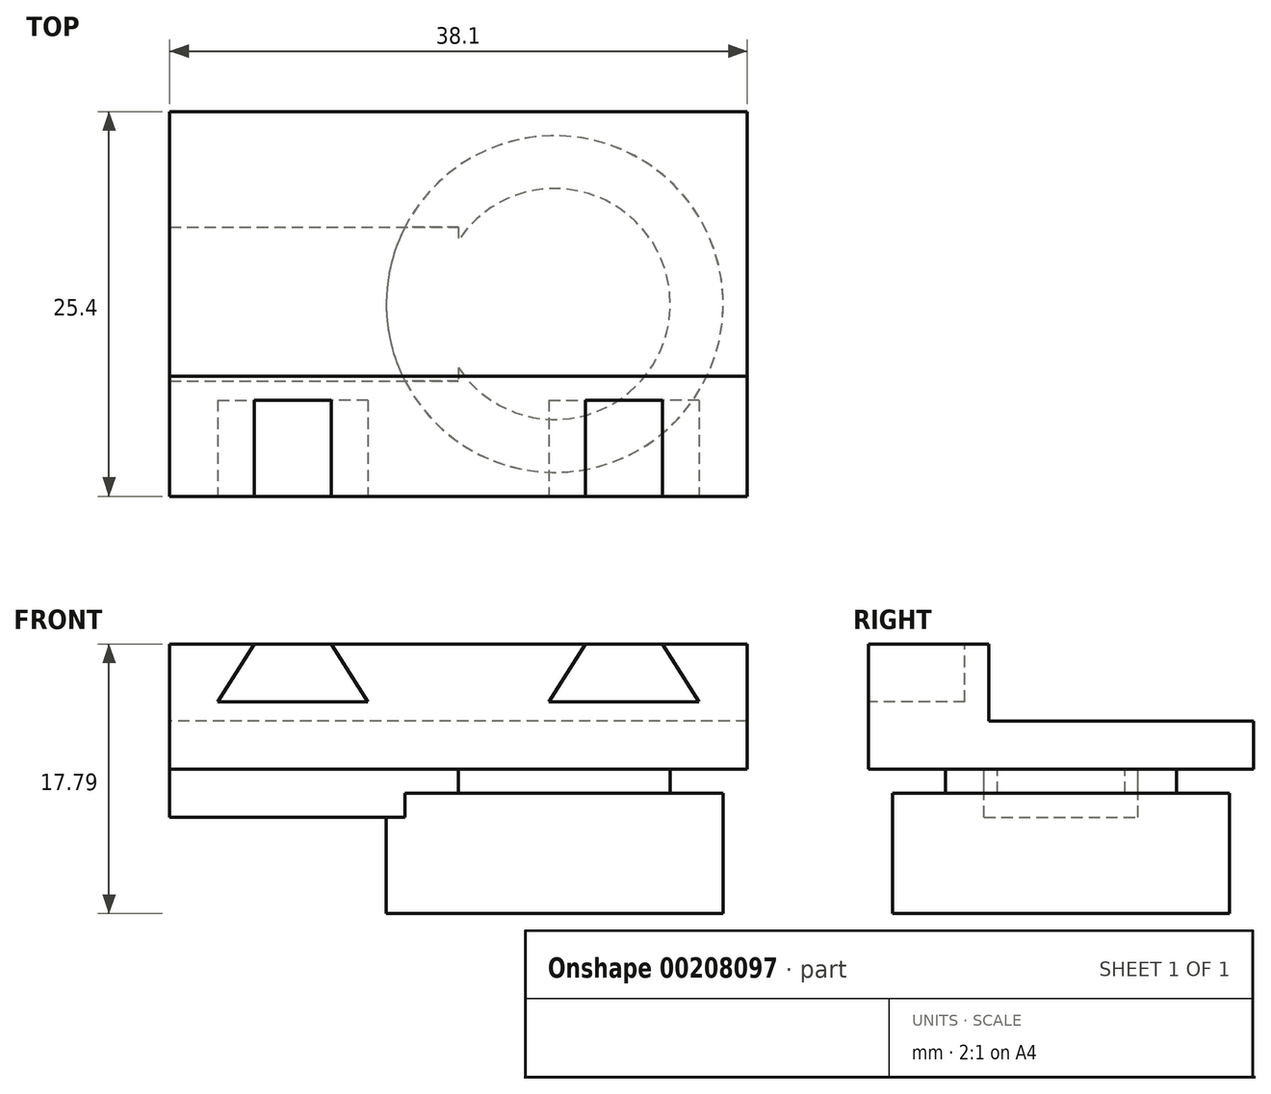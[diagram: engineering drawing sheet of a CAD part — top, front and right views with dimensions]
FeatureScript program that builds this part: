
annotation { "Feature Type Name" : "Feature", "Feature Type Description" : "" }
export const myFeature = defineFeature(function(context is Context, id is Id, definition is map)
    precondition{}
    {
        {
            var Q0;
            Q0=qCreatedBy(makeId("Top.planeOp"),FACE);
            var sketch = newSketch(context, id + "F0", { "sketchPlane" : qUnion([Q0])});
            skLineSegment(sketch, "E0.bottom", {"start": v(0, 0) * mm, "end": v(-38.1, 0) * mm});
            skLineSegment(sketch, "E0.top", {"start": v(0, 25.4) * mm, "end": v(-38.1, 25.4) * mm});
            skLineSegment(sketch, "E0.left", {"start": v(0, 0) * mm, "end": v(0, 25.4) * mm});
            skLineSegment(sketch, "E0.right", {"start": v(-38.1, 0) * mm, "end": v(-38.1, 25.4) * mm});
            skSolve(sketch);
        }
        {
            var Q0;
            Q0=makeQuery(id+"F0.imprint","IMPRINT",FACE,{"disambiguationData":[TD([[makeQuery(id+"F0.imprint","IMPRINT",EDGE,{"derivedFrom":sQuery(id+"F0.wireOp",EDGE,"E0.bottom")}),-1.0]])]});
            extrude(context, id + "F1", {"entities" : qUnion([Q0]), "depth" : 3.17 * mm});
        }
        {
            var Q0;
            Q0=makeQuery(id+"F1.opExtrude","SWEPT_FACE",FACE,{"disambiguationData":[OSD([sQuery(id+"F0.wireOp",EDGE,"E0.bottom")])]});
            var sketch = newSketch(context, id + "F2", { "sketchPlane" : qUnion([Q0])});
            skLineSegment(sketch, "E1.bottom", {"start": v(-38.1, 3.17) * mm, "end": v(0, 3.18) * mm});
            skLineSegment(sketch, "E1.left", {"start": v(-38.1, 3.18) * mm, "end": v(-38.1, 8.26) * mm});
            skLineSegment(sketch, "E1.right", {"start": v(0, 3.18) * mm, "end": v(0, 8.26) * mm});
            skLineSegment(sketch, "E2", {"start": v(-38.1, 8.26) * mm, "end": v(-32.51, 8.26) * mm});
            skLineSegment(sketch, "E3", {"start": v(-34.93, 4.45) * mm, "end": v(-25.02, 4.45) * mm});
            skLineSegment(sketch, "E4", {"start": v(-25.02, 4.45) * mm, "end": v(-27.43, 8.26) * mm});
            skLineSegment(sketch, "E5", {"start": v(-10.67, 8.25) * mm, "end": v(-13.08, 4.45) * mm});
            skLineSegment(sketch, "E6", {"start": v(-13.08, 4.45) * mm, "end": v(-3.18, 4.45) * mm});
            skLineSegment(sketch, "E7", {"start": v(-3.17, 4.44) * mm, "end": v(-5.59, 8.25) * mm});
            skLineSegment(sketch, "E8", {"start": v(-5.59, 8.26) * mm, "end": v(0, 8.26) * mm});
            skLineSegment(sketch, "E9", {"start": v(-27.43, 8.25) * mm, "end": v(-10.67, 8.26) * mm});
            skLineSegment(sketch, "E10", {"start": v(-34.93, 4.45) * mm, "end": v(-32.51, 8.25) * mm});
            skSolve(sketch);
        }
        {
            var Q0;
            Q0=makeQuery(id+"F2.imprint","IMPRINT",FACE,{"disambiguationData":[TD([[makeQuery(id+"F2.imprint","IMPRINT",EDGE,{"derivedFrom":sQuery(id+"F2.wireOp",EDGE,"E1.bottom")}),-1.0]])]});
            extrude(context, id + "F3", {"entities" : qUnion([Q0]), "operationType" : NewBodyOperationType.ADD, "oppositeDirection" : true, "depth" : 6.35 * mm});
        }
        {
            var Q0;
            Q0=makeQuery(id+"F1.opExtrude","CAP_FACE",FACE,{"disambiguationData":[OSD([sQuery(id+"F0.wireOp",EDGE,"E0.bottom"),sQuery(id+"F0.wireOp",EDGE,"E0.top"),sQuery(id+"F0.wireOp",EDGE,"E0.left"),sQuery(id+"F0.wireOp",EDGE,"E0.right")])],"isStart":false});
            var sketch = newSketch(context, id + "F4", { "sketchPlane" : qUnion([Q0])});
            skLineSegment(sketch, "E11.bottom", {"start": v(0, 6.35) * mm, "end": v(-38.1, 6.35) * mm});
            skLineSegment(sketch, "E11.top", {"start": v(0, 7.94) * mm, "end": v(-38.1, 7.94) * mm});
            skLineSegment(sketch, "E11.left", {"start": v(0, 6.35) * mm, "end": v(0, 7.94) * mm});
            skLineSegment(sketch, "E11.right", {"start": v(-38.1, 6.35) * mm, "end": v(-38.1, 7.94) * mm});
            skSolve(sketch);
        }
        {
            var Q0;
            Q0=makeQuery(id+"F4.imprint","IMPRINT",FACE,{"disambiguationData":[TD([[makeQuery(id+"F4.imprint","IMPRINT",EDGE,{"derivedFrom":sQuery(id+"F4.wireOp",EDGE,"E11.bottom")}),-1.0]])]});
            var Q1;
            Q1=makeQuery(id+"F3.opExtrude","SWEPT_FACE",FACE,{"disambiguationData":[OSD([sQuery(id+"F2.wireOp",EDGE,"E9")])]});
            extrude(context, id + "F5", {"entities" : qUnion([Q0]), "operationType" : NewBodyOperationType.ADD, "endBound" : BoundingType.UP_TO_SURFACE, "endBoundEntityFace" : qUnion([Q1]), "depth" : 25.4 * mm});
        }
        {
            var Q0;
            Q0=makeQuery(id+"F1.opExtrude","CAP_FACE",FACE,{"disambiguationData":[OSD([sQuery(id+"F0.wireOp",EDGE,"E0.bottom"),sQuery(id+"F0.wireOp",EDGE,"E0.top"),sQuery(id+"F0.wireOp",EDGE,"E0.left"),sQuery(id+"F0.wireOp",EDGE,"E0.right")])],"isStart":true});
            var sketch = newSketch(context, id + "F6", { "sketchPlane" : qUnion([Q0])});
            skCircle(sketch, "E12", {"center": v(-12.7, -12.7) * mm, "radius": 11.11 * mm});
            skSolve(sketch);
        }
        {
            var Q0;
            Q0 = qSketchRegion(id + "F6", true);
            extrude(context, id + "F7", {"entities" : qUnion([Q0]), "operationType" : NewBodyOperationType.ADD, "depth" : 9.52 * mm});
        }
        {
            var Q0;
            Q0=makeQuery(id+"F1.opExtrude","CAP_FACE",FACE,{"disambiguationData":[OSD([sQuery(id+"F0.wireOp",EDGE,"E0.bottom"),sQuery(id+"F0.wireOp",EDGE,"E0.top"),sQuery(id+"F0.wireOp",EDGE,"E0.left"),sQuery(id+"F0.wireOp",EDGE,"E0.right")])],"isStart":true});
            var sketch = newSketch(context, id + "F8", { "sketchPlane" : qUnion([Q0])});
            skCircle(sketch, "E13", {"center": v(-12.7, -12.7) * mm, "radius": 11.43 * mm});
            skCircle(sketch, "E14", {"center": v(-12.7, -12.7) * mm, "radius": 7.62 * mm});
            skSolve(sketch);
        }
        {
            var Q0;
            Q0 = qSketchRegion(id + "F8", true);
            extrude(context, id + "F9", {"entities" : qUnion([Q0]), "operationType" : NewBodyOperationType.REMOVE, "depth" : 1.59 * mm});
        }
        {
            var Q0;
            Q0=makeQuery(id+"F9.boolean.opBoolean","MERGE",FACE,{"derivedFrom":[makeQuery(id+"F1.opExtrude","CAP_FACE",FACE,{"disambiguationData":[OSD([sQuery(id+"F0.wireOp",EDGE,"E0.bottom"),sQuery(id+"F0.wireOp",EDGE,"E0.top"),sQuery(id+"F0.wireOp",EDGE,"E0.left"),sQuery(id+"F0.wireOp",EDGE,"E0.right")])],"isStart":true}),makeQuery(id+"F9.opExtrude","CAP_FACE",FACE,{"disambiguationData":[OSD([sQuery(id+"F8.wireOp",EDGE,"E13"),sQuery(id+"F8.wireOp",EDGE,"E14")])],"isStart":true})]});
            var sketch = newSketch(context, id + "F10", { "sketchPlane" : qUnion([Q0])});
            skLineSegment(sketch, "E15.bottom", {"start": v(-38.1, -7.62) * mm, "end": v(-19.05, -7.62) * mm});
            skLineSegment(sketch, "E15.top", {"start": v(-38.1, -17.78) * mm, "end": v(-19.05, -17.78) * mm});
            skLineSegment(sketch, "E15.left", {"start": v(-38.1, -7.62) * mm, "end": v(-38.1, -17.78) * mm});
            skLineSegment(sketch, "E15.right", {"start": v(-19.05, -7.62) * mm, "end": v(-19.05, -17.78) * mm});
            skSolve(sketch);
        }
        {
            var Q0;
            Q0 = qSketchRegion(id + "F10", true);
            extrude(context, id + "F11", {"entities" : qUnion([Q0]), "operationType" : NewBodyOperationType.ADD, "depth" : 3.17 * mm});
        }
    });
